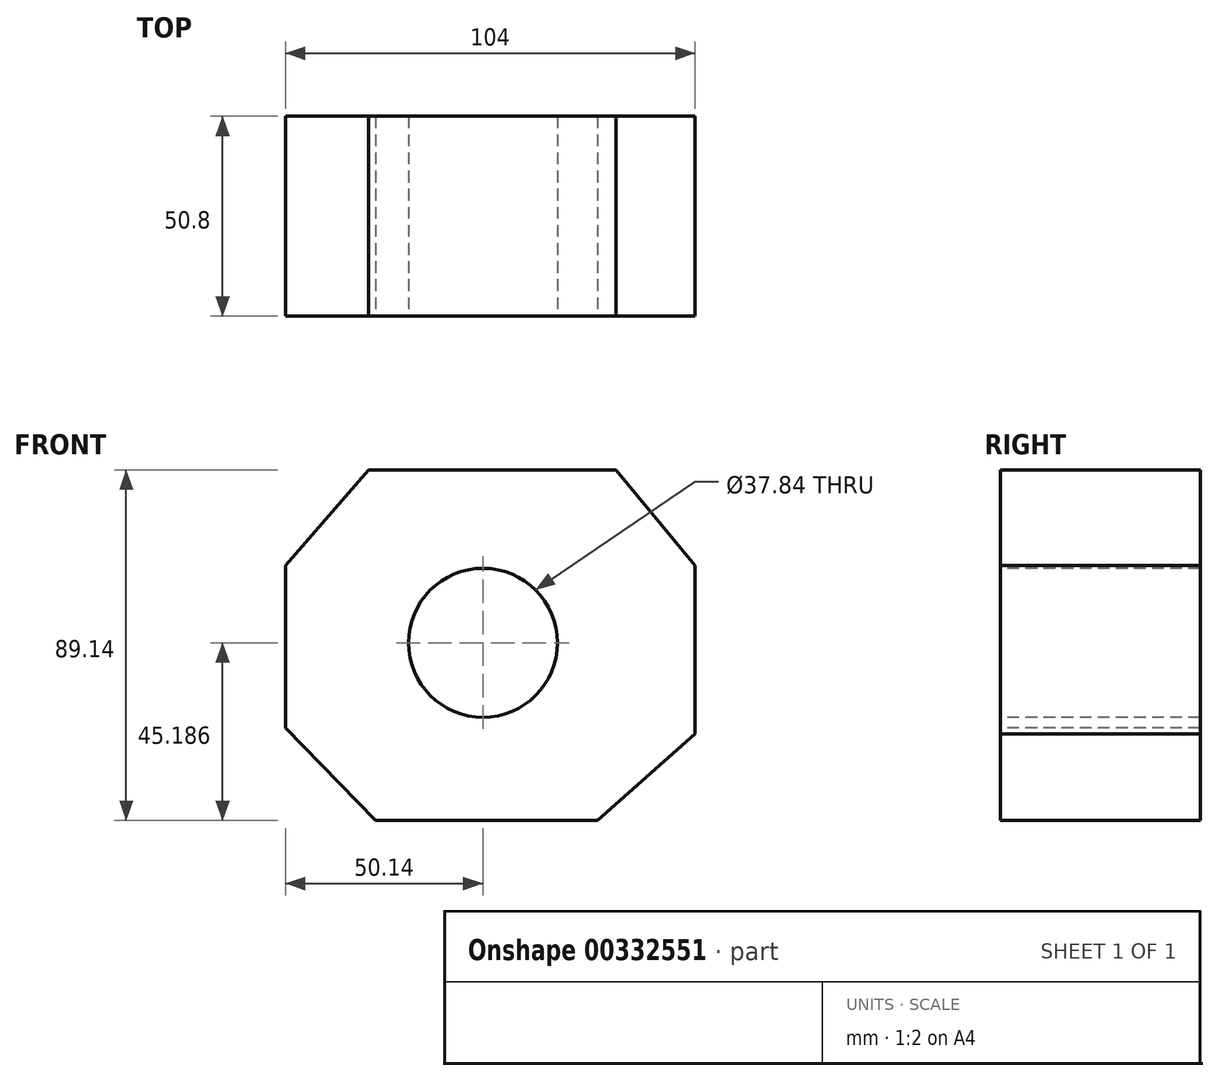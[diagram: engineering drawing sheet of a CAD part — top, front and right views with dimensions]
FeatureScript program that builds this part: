
annotation { "Feature Type Name" : "Feature", "Feature Type Description" : "" }
export const myFeature = defineFeature(function(context is Context, id is Id, definition is map)
    precondition{}
    {
        {
            var Q0;
            Q0=qCreatedBy(makeId("Front.planeOp"),FACE);
            var sketch = newSketch(context, id + "F0", { "sketchPlane" : qUnion([Q0])});
            skLineSegment(sketch, "E0.bottom", {"start": v(-50.14, 24.3) * mm, "end": v(53.86, 24.3) * mm});
            skLineSegment(sketch, "E0.top", {"start": v(-50.14, -64.84) * mm, "end": v(53.86, -64.84) * mm});
            skLineSegment(sketch, "E0.left", {"start": v(-50.14, 24.3) * mm, "end": v(-50.14, -64.84) * mm});
            skLineSegment(sketch, "E0.right", {"start": v(53.86, 24.3) * mm, "end": v(53.86, -64.84) * mm});
            skSolve(sketch);
        }
        {
            var Q0;
            Q0=makeQuery(id+"F0.imprint","IMPRINT",FACE,{"disambiguationData":[TD([[makeQuery(id+"F0.imprint","IMPRINT",EDGE,{"derivedFrom":sQuery(id+"F0.wireOp",EDGE,"E0.bottom")}),-1.0]])]});
            extrude(context, id + "F1", {"entities" : qUnion([Q0]), "depth" : 50.8 * mm});
        }
        {
            var Q0;
            Q0=makeQuery(id+"F1.opExtrude","CAP_FACE",FACE,{"disambiguationData":[OSD([sQuery(id+"F0.wireOp",EDGE,"E0.bottom"),sQuery(id+"F0.wireOp",EDGE,"E0.top"),sQuery(id+"F0.wireOp",EDGE,"E0.left"),sQuery(id+"F0.wireOp",EDGE,"E0.right")])],"isStart":false});
            var sketch = newSketch(context, id + "F2", { "sketchPlane" : qUnion([Q0])});
            skCircle(sketch, "E1", {"center": v(0, -19.65) * mm, "radius": 18.92 * mm});
            skPoint(sketch, "E2.center.orphan", {"position": v(0, -11.92) * mm});
            skSolve(sketch);
        }
        {
            var Q0;
            Q0=makeQuery(id+"F2.imprint","IMPRINT",FACE,{"disambiguationData":[TD([[makeQuery(id+"F2.imprint","IMPRINT",EDGE,{"derivedFrom":sQuery(id+"F2.wireOp",EDGE,"E1")}),1.0]])]});
            extrude(context, id + "F3", {"entities" : qUnion([Q0]), "operationType" : NewBodyOperationType.REMOVE, "endBound" : BoundingType.THROUGH_ALL, "oppositeDirection" : true, "depth" : 25.4 * mm});
        }
        {
            var Q0;
            Q0=makeQuery(id+"F1.opExtrude","CAP_FACE",FACE,{"disambiguationData":[OSD([sQuery(id+"F0.wireOp",EDGE,"E0.bottom"),sQuery(id+"F0.wireOp",EDGE,"E0.top"),sQuery(id+"F0.wireOp",EDGE,"E0.left"),sQuery(id+"F0.wireOp",EDGE,"E0.right")])],"isStart":false});
            var sketch = newSketch(context, id + "F4", { "sketchPlane" : qUnion([Q0])});
            skLineSegment(sketch, "E3", {"start": v(-50.14, 0) * mm, "end": v(-29.1, 24.3) * mm});
            skLineSegment(sketch, "E4", {"start": v(53.86, 0) * mm, "end": v(33.74, 24.3) * mm});
            skLineSegment(sketch, "E5", {"start": v(-50.14, -41.32) * mm, "end": v(-27.24, -64.84) * mm});
            skLineSegment(sketch, "E6", {"start": v(29.1, -64.84) * mm, "end": v(53.86, -42.87) * mm});
            skSolve(sketch);
        }
        {
            var Q0;
            {var subQ0=sQuery(id+"F4.wireOp",EDGE,"E3");Q0=makeQuery(id+"F4.imprint","IMPRINT",FACE,{"disambiguationData":[TD([[makeQuery(id+"F4.imprint","IMPRINT",EDGE,{"derivedFrom":subQ0}),1.0]])]});}
            var Q1;
            {var subQ0=sQuery(id+"F4.wireOp",EDGE,"E4");Q1=makeQuery(id+"F4.imprint","IMPRINT",FACE,{"disambiguationData":[TD([[makeQuery(id+"F4.imprint","IMPRINT",EDGE,{"derivedFrom":subQ0}),-1.0]])]});}
            var Q2;
            {var subQ0=sQuery(id+"F4.wireOp",EDGE,"E5");Q2=makeQuery(id+"F4.imprint","IMPRINT",FACE,{"disambiguationData":[TD([[makeQuery(id+"F4.imprint","IMPRINT",EDGE,{"derivedFrom":subQ0}),-1.0]])]});}
            var Q3;
            {var subQ0=sQuery(id+"F4.wireOp",EDGE,"E6");Q3=makeQuery(id+"F4.imprint","IMPRINT",FACE,{"disambiguationData":[TD([[makeQuery(id+"F4.imprint","IMPRINT",EDGE,{"derivedFrom":subQ0}),-1.0]])]});}
            extrude(context, id + "F5", {"entities" : qUnion([Q0, Q1, Q2, Q3]), "operationType" : NewBodyOperationType.REMOVE, "endBound" : BoundingType.THROUGH_ALL, "oppositeDirection" : true, "depth" : 25.4 * mm});
        }
    });
